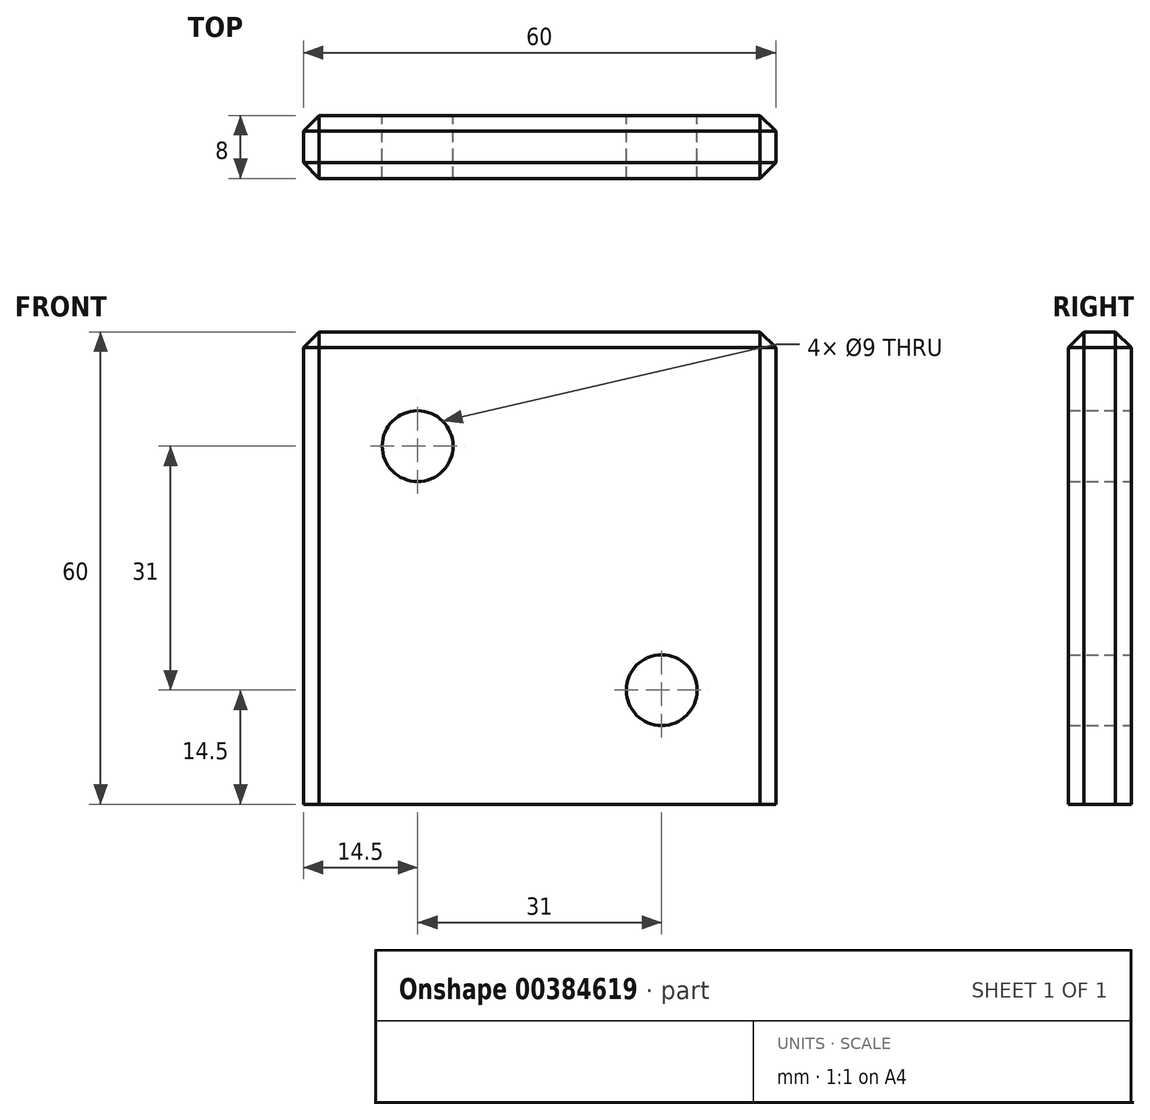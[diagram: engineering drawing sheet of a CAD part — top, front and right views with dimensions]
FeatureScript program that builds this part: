
annotation { "Feature Type Name" : "Feature", "Feature Type Description" : "" }
export const myFeature = defineFeature(function(context is Context, id is Id, definition is map)
    precondition{}
    {
        {
            var Q0;
            Q0=qCreatedBy(makeId("Front.planeOp"),FACE);
            var sketch = newSketch(context, id + "F0", { "sketchPlane" : qUnion([Q0])});
            skLineSegment(sketch, "E0.bottom", {"start": v(-30, -30) * mm, "end": v(30, -30) * mm});
            skLineSegment(sketch, "E0.top", {"start": v(-30, 30) * mm, "end": v(30, 30) * mm});
            skLineSegment(sketch, "E0.left", {"start": v(-30, -30) * mm, "end": v(-30, 30) * mm});
            skLineSegment(sketch, "E0.right", {"start": v(30, -30) * mm, "end": v(30, 30) * mm});
            skPoint(sketch, "E0.middle", {"position": v(0, 0) * mm});
            skCircle(sketch, "E1", {"center": v(-15.5, 15.5) * mm, "radius": 4.5 * mm});
            skCircle(sketch, "E2", {"center": v(15.5, -15.5) * mm, "radius": 4.5 * mm});
            skPoint(sketch, "E3.orphan", {"position": v(-15.5, -15.5) * mm});
            skPoint(sketch, "E4.orphan", {"position": v(15.5, 15.5) * mm});
            skSolve(sketch);
        }
        {
            var Q0;
            Q0=qSketchRegion(id+"F0",true);
            extrude(context, id + "F1", {"entities" : qUnion([Q0]), "endBound" : BoundingType.SYMMETRIC, "depth" : 8 * mm});
        }
        {
            var Q0;
            Q0=makeQuery(id+"F1.opExtrude","CAP_EDGE",EDGE,{"disambiguationData":[OSD([sQuery(id+"F0.wireOp",EDGE,"E0.right")])],"isStart":false});
            var Q1;
            Q1=makeQuery(id+"F1.opExtrude","CAP_EDGE",EDGE,{"disambiguationData":[OSD([sQuery(id+"F0.wireOp",EDGE,"E0.right")])],"isStart":true});
            var Q2;
            Q2=makeQuery(id+"F1.opExtrude","SWEPT_EDGE",EDGE,{"disambiguationData":[OSD([sQuery(id+"F0.wireOp",EDGE,"E0.top"),sQuery(id+"F0.wireOp",EDGE,"E0.right")])]});
            var Q3;
            Q3=makeQuery(id+"F1.opExtrude","CAP_EDGE",EDGE,{"disambiguationData":[OSD([sQuery(id+"F0.wireOp",EDGE,"E0.top")])],"isStart":false});
            var Q4;
            Q4=makeQuery(id+"F1.opExtrude","CAP_EDGE",EDGE,{"disambiguationData":[OSD([sQuery(id+"F0.wireOp",EDGE,"E0.top")])],"isStart":true});
            var Q5;
            Q5=makeQuery(id+"F1.opExtrude","CAP_EDGE",EDGE,{"disambiguationData":[OSD([sQuery(id+"F0.wireOp",EDGE,"E0.left")])],"isStart":false});
            var Q6;
            Q6=makeQuery(id+"F1.opExtrude","SWEPT_EDGE",EDGE,{"disambiguationData":[OSD([sQuery(id+"F0.wireOp",EDGE,"E0.top"),sQuery(id+"F0.wireOp",EDGE,"E0.left")])]});
            var Q7;
            Q7=makeQuery(id+"F1.opExtrude","CAP_EDGE",EDGE,{"disambiguationData":[OSD([sQuery(id+"F0.wireOp",EDGE,"E0.left")])],"isStart":true});
            chamfer(context, id + "F2", {"entities" : qUnion([Q0, Q1, Q2, Q3, Q4, Q5, Q6, Q7]), "width" : 2 * mm, "tangentPropagation" : true});
        }
    });
